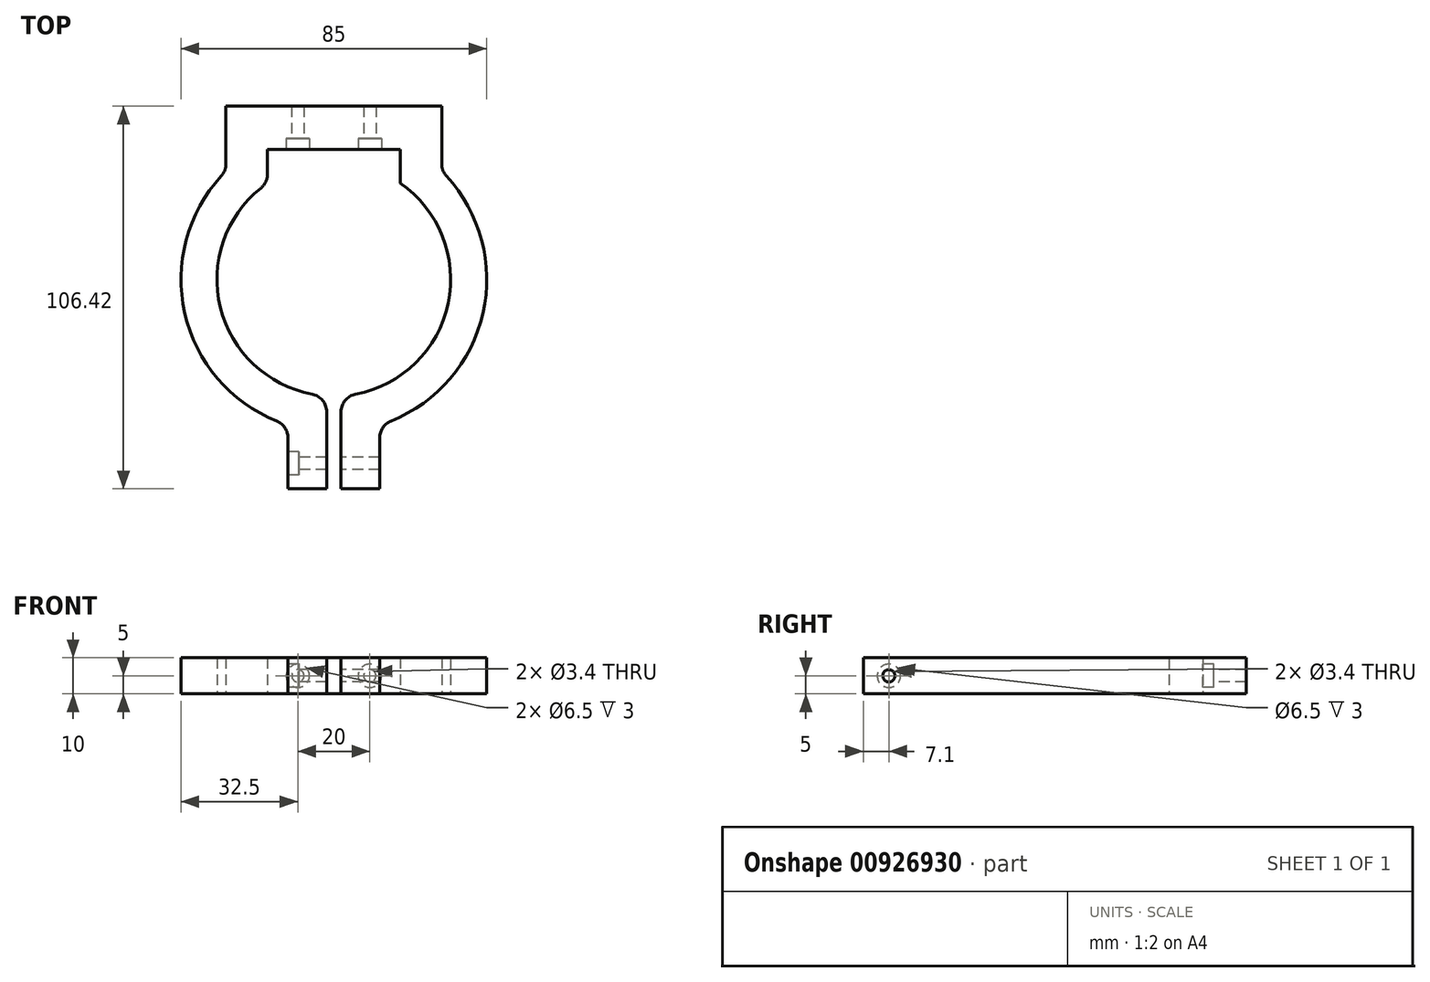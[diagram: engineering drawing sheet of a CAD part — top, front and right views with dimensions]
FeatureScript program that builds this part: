
annotation { "Feature Type Name" : "Feature", "Feature Type Description" : "" }
export const myFeature = defineFeature(function(context is Context, id is Id, definition is map)
    precondition{}
    {
        {
            var Q0;
            Q0=qCreatedBy(makeId("Top.planeOp"),FACE);
            var sketch = newSketch(context, id + "F0", { "sketchPlane" : qUnion([Q0])});
            skArc(sketch, "E0", {"start": v(6.07, -31.93) * mm, "mid": v(31.8, -6.7) * mm, "end": v(18.44, 26.77) * mm});
            skLineSegment(sketch, "E1", {"start": v(0, 81.42) * mm, "end": v(0, 36.16) * mm, "construction": true});
            skLineSegment(sketch, "E2.bottom", {"start": v(12.74, -58.26) * mm, "end": v(2, -58.26) * mm});
            skLineSegment(sketch, "E2.left", {"start": v(12.74, -58.26) * mm, "end": v(12.74, -44.06) * mm});
            skLineSegment(sketch, "E2.right", {"start": v(-12.74, -58.26) * mm, "end": v(-12.74, -44.06) * mm});
            skLineSegment(sketch, "E3.bottom", {"start": v(2, -102.06) * mm, "end": v(-2, -102.06) * mm});
            skLineSegment(sketch, "E3.left", {"start": v(2, -58.26) * mm, "end": v(2, -36.84) * mm});
            skLineSegment(sketch, "E3.right", {"start": v(-2, -58.26) * mm, "end": v(-2, -36.84) * mm});
            skArc(sketch, "E4.trimOffspring", {"start": v(15.87, -39.42) * mm, "mid": v(41.45, -9.4) * mm, "end": v(31.32, 28.73) * mm});
            skLineSegment(sketch, "E5.trimOffspring", {"start": v(-2, -58.26) * mm, "end": v(-12.74, -58.26) * mm});
            skLineSegment(sketch, "E6.top", {"start": v(30, 48.16) * mm, "end": v(-30, 48.16) * mm});
            skLineSegment(sketch, "E6.right", {"start": v(-30, 32.11) * mm, "end": v(-30, 48.16) * mm});
            skLineSegment(sketch, "E7.trimOffspring", {"start": v(30, 32.11) * mm, "end": v(30, 48.16) * mm});
            skArc(sketch, "E8.trimOffspring", {"start": v(-31.32, 28.73) * mm, "mid": v(-41.45, -9.4) * mm, "end": v(-15.87, -39.42) * mm});
            skPoint(sketch, "E9.visualSharp", {"position": v(-30, 30.1) * mm});
            skArc(sketch, "E9.filletArc", {"start": v(-31.32, 28.73) * mm, "mid": v(-30.34, 30.3) * mm, "end": v(-30, 32.11) * mm});
            skPoint(sketch, "E10.visualSharp", {"position": v(30, 30.1) * mm});
            skArc(sketch, "E10.filletArc", {"start": v(30, 32.11) * mm, "mid": v(30.34, 30.3) * mm, "end": v(31.32, 28.73) * mm});
            skPoint(sketch, "E11.visualSharp", {"position": v(-2, -32.44) * mm});
            skArc(sketch, "E11.filletArc", {"start": v(-2, -36.84) * mm, "mid": v(-3.15, -33.65) * mm, "end": v(-6.07, -31.93) * mm});
            skPoint(sketch, "E12.visualSharp", {"position": v(2, -32.44) * mm});
            skArc(sketch, "E12.filletArc", {"start": v(6.07, -31.93) * mm, "mid": v(3.15, -33.65) * mm, "end": v(2, -36.84) * mm});
            skPoint(sketch, "E13.visualSharp", {"position": v(12.74, -40.55) * mm});
            skArc(sketch, "E13.filletArc", {"start": v(15.87, -39.42) * mm, "mid": v(13.6, -41.26) * mm, "end": v(12.74, -44.06) * mm});
            skPoint(sketch, "E14.visualSharp", {"position": v(-12.74, -40.55) * mm});
            skArc(sketch, "E14.filletArc", {"start": v(-12.74, -44.06) * mm, "mid": v(-13.6, -41.26) * mm, "end": v(-15.87, -39.42) * mm});
            skLineSegment(sketch, "E15.top", {"start": v(18.44, 36.16) * mm, "end": v(-18.44, 36.16) * mm});
            skLineSegment(sketch, "E15.left", {"start": v(18.44, 26.77) * mm, "end": v(18.44, 36.16) * mm});
            skLineSegment(sketch, "E15.right", {"start": v(-18.44, 29.28) * mm, "end": v(-18.44, 36.16) * mm});
            skArc(sketch, "E16.trimOffspring", {"start": v(-20.31, 25.37) * mm, "mid": v(-31.54, -7.84) * mm, "end": v(-6.07, -31.93) * mm});
            skLineSegment(sketch, "E17.trimOffspring", {"start": v(0, 32.5) * mm, "end": v(0, -61.77) * mm, "construction": true});
            skPoint(sketch, "E18.visualSharp", {"position": v(18.44, 26.77) * mm});
            skLineSegment(sketch, "E18.filletArc", {"start": v(18.44, 26.77) * mm, "end": v(18.44, 26.77) * mm});
            skPoint(sketch, "E19.visualSharp", {"position": v(-18.44, 26.77) * mm});
            skLineSegment(sketch, "E19.filletArc", {"start": v(-18.44, 26.77) * mm, "end": v(-18.44, 26.77) * mm});
            skPoint(sketch, "E20.visualSharp", {"position": v(18.44, 36.16) * mm});
            skLineSegment(sketch, "E20.filletArc", {"start": v(18.44, 36.16) * mm, "end": v(18.44, 36.16) * mm});
            skArc(sketch, "E21.filletArc", {"start": v(-20.31, 25.37) * mm, "mid": v(-18.93, 27.1) * mm, "end": v(-18.44, 29.28) * mm});
            skSolve(sketch);
        }
        {
            var Q0;
            Q0=makeQuery(id+"F0.imprint","IMPRINT",FACE,{"disambiguationData":[TD([[makeQuery(id+"F0.imprint","IMPRINT",EDGE,{"derivedFrom":sQuery(id+"F0.wireOp",EDGE,"E0")}),-1.0]])]});
            extrude(context, id + "F1", {"entities" : qUnion([Q0]), "depth" : 10 * mm, "offsetDistance" : 25 * mm});
        }
        {
            var Q0;
            Q0=makeQuery(id+"F1.opExtrude","SWEPT_FACE",FACE,{"disambiguationData":[OSD([sQuery(id+"F0.wireOp",EDGE,"E2.right")])]});
            var sketch = newSketch(context, id + "F2", { "sketchPlane" : qUnion([Q0])});
            skPoint(sketch, "E22", {"position": v(51.16, 5) * mm});
            skPoint(sketch, "E22.positionSnap0", {"position": v(58.26, 5) * mm});
            skPoint(sketch, "E22.positionSnap1", {"position": v(51.16, 0) * mm});
            skSolve(sketch);
        }
        {
            var Q0;
            Q0=sQuery(id+"F2.wireOp",VERTEX,"E22");
            var Q1;
            Q1=makeQuery(id+"F1.opExtrude","SWEPT_BODY",BODY,{"disambiguationData":[OSD([sQuery(id+"F0.wireOp",EDGE,"E0"),sQuery(id+"F0.wireOp",EDGE,"E2.bottom"),sQuery(id+"F0.wireOp",EDGE,"E2.left"),sQuery(id+"F0.wireOp",EDGE,"E2.right"),sQuery(id+"F0.wireOp",EDGE,"E3.left"),sQuery(id+"F0.wireOp",EDGE,"E3.right"),sQuery(id+"F0.wireOp",EDGE,"E4.trimOffspring"),sQuery(id+"F0.wireOp",EDGE,"E5.trimOffspring"),sQuery(id+"F0.wireOp",EDGE,"E6.top"),sQuery(id+"F0.wireOp",EDGE,"E6.right"),sQuery(id+"F0.wireOp",EDGE,"E7.trimOffspring"),sQuery(id+"F0.wireOp",EDGE,"E8.trimOffspring"),sQuery(id+"F0.wireOp",EDGE,"E9.filletArc"),sQuery(id+"F0.wireOp",EDGE,"E10.filletArc"),sQuery(id+"F0.wireOp",EDGE,"E11.filletArc"),sQuery(id+"F0.wireOp",EDGE,"E12.filletArc"),sQuery(id+"F0.wireOp",EDGE,"E13.filletArc"),sQuery(id+"F0.wireOp",EDGE,"E14.filletArc"),sQuery(id+"F0.wireOp",EDGE,"E15.top"),sQuery(id+"F0.wireOp",EDGE,"E15.left"),sQuery(id+"F0.wireOp",EDGE,"E15.right"),sQuery(id+"F0.wireOp",EDGE,"E16.trimOffspring"),sQuery(id+"F0.wireOp",EDGE,"E21.filletArc")])]});
            hole(context, id + "F3", {"style" : HoleStyle.C_BORE, "endStyle" : HoleEndStyle.THROUGH, "standardTappedOrClearance" : lookupTablePath({ "fit" : "Normal", "standard" : "ISO", "size" : "M3", "type" : "Clearance" }), "standardBlindInLast" : lookupTablePath({ "fit" : "Normal", "standard" : "ISO", "size" : "M3", "type" : "Clearance" }), "holeDiameter" : 3.4 * mm, "cBoreDiameter" : 6.5 * mm, "cBoreDepth" : 3 * mm, "majorDiameter" : 5 * mm, "isTappedThrough" : true, "tappedDepth" : 12 * mm, "tapClearance" : 3, "locations" : qUnion([Q0]), "scope" : qUnion([Q1])});
        }
        {
            var Q0;
            Q0=makeQuery(id+"F1.opExtrude","SWEPT_FACE",FACE,{"disambiguationData":[OSD([sQuery(id+"F0.wireOp",EDGE,"E15.top")])]});
            var sketch = newSketch(context, id + "F4", { "sketchPlane" : qUnion([Q0])});
            skPoint(sketch, "E23", {"position": v(10, 5) * mm});
            skPoint(sketch, "E24.MirrorP", {"position": v(-10, 5) * mm});
            skSolve(sketch);
        }
        {
            var Q0;
            Q0=sQuery(id+"F4.wireOp",VERTEX,"E23");
            var Q1;
            Q1=sQuery(id+"F4.wireOp",VERTEX,"E24.MirrorP");
            var Q2;
            Q2=makeQuery(id+"F1.opExtrude","SWEPT_BODY",BODY,{"disambiguationData":[OSD([sQuery(id+"F0.wireOp",EDGE,"E0"),sQuery(id+"F0.wireOp",EDGE,"E2.bottom"),sQuery(id+"F0.wireOp",EDGE,"E2.left"),sQuery(id+"F0.wireOp",EDGE,"E2.right"),sQuery(id+"F0.wireOp",EDGE,"E3.left"),sQuery(id+"F0.wireOp",EDGE,"E3.right"),sQuery(id+"F0.wireOp",EDGE,"E4.trimOffspring"),sQuery(id+"F0.wireOp",EDGE,"E5.trimOffspring"),sQuery(id+"F0.wireOp",EDGE,"E6.top"),sQuery(id+"F0.wireOp",EDGE,"E6.right"),sQuery(id+"F0.wireOp",EDGE,"E7.trimOffspring"),sQuery(id+"F0.wireOp",EDGE,"E8.trimOffspring"),sQuery(id+"F0.wireOp",EDGE,"E9.filletArc"),sQuery(id+"F0.wireOp",EDGE,"E10.filletArc"),sQuery(id+"F0.wireOp",EDGE,"E11.filletArc"),sQuery(id+"F0.wireOp",EDGE,"E12.filletArc"),sQuery(id+"F0.wireOp",EDGE,"E13.filletArc"),sQuery(id+"F0.wireOp",EDGE,"E14.filletArc"),sQuery(id+"F0.wireOp",EDGE,"E15.top"),sQuery(id+"F0.wireOp",EDGE,"E15.left"),sQuery(id+"F0.wireOp",EDGE,"E15.right"),sQuery(id+"F0.wireOp",EDGE,"E16.trimOffspring"),sQuery(id+"F0.wireOp",EDGE,"E21.filletArc")])]});
            hole(context, id + "F5", {"style" : HoleStyle.C_BORE, "endStyle" : HoleEndStyle.THROUGH, "standardTappedOrClearance" : lookupTablePath({ "fit" : "Normal", "standard" : "ISO", "size" : "M3", "type" : "Clearance" }), "standardBlindInLast" : lookupTablePath({ "fit" : "Normal", "standard" : "ISO", "size" : "M3", "type" : "Clearance" }), "holeDiameter" : 3.4 * mm, "cBoreDiameter" : 6.5 * mm, "cBoreDepth" : 3 * mm, "majorDiameter" : 5 * mm, "isTappedThrough" : true, "tappedDepth" : 12 * mm, "tapClearance" : 3, "locations" : qUnion([Q0, Q1]), "scope" : qUnion([Q2])});
        }
    });
